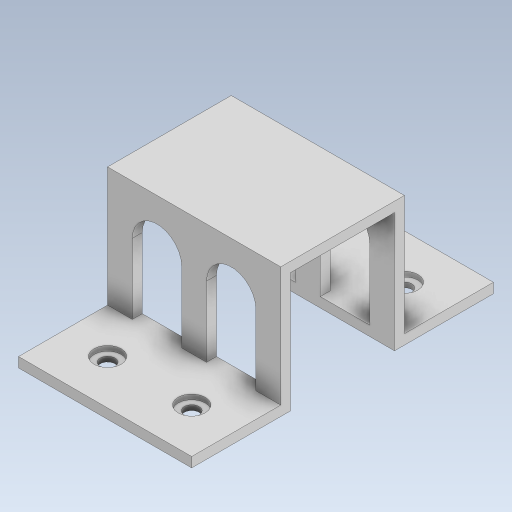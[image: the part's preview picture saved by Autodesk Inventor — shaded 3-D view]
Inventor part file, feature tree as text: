
AUTODESK INVENTOR PART (.ipt)
format: ipt  version: 2023.5 (Build 275446000, 446)  size: 423,424 bytes
history: native  units: in
note: dims shown in document units (in); Inventor stores cm internally (conversion verified against a paired STEP export)
features: extrude x10, sketch x8
ambient origin geometry x8: Origin, YZ Plane, XZ Plane, XY Plane, X Axis, Y Axis, Z Axis, Center Point
bodies: Solid1 (feature_tree)
feature tree (18):
  extrude  "Extrusion1"  Depth=0.7874in
  extrude  "Extrusion2"  Depth=0.0787in
  extrude  "Extrusion3"  Depth=0.0787in
  extrude  "Extrusion4"  Depth=0.0787in
  extrude  "Extrusion5"  Depth=0.7087in TaperAngle=0.0deg
  sketch  "Sketch6"  dims[d15=0.1181in d16=0.3543in]
  extrude  "Extrusion6"  Depth=0.3543in
  extrude  "Extrusion7"  Depth=0.1181in
  sketch  "Sketch7"  dims[d17=0.3543in d18=0.1181in]
  extrude  "Extrusion8"  Depth=0.9843in
  extrude  "Extrusion9"  Depth=0.9843in
  extrude  "Extrusion10"  Depth=0.0787in TaperAngle=0.0deg
  sketch  "Sketch1"  dims[d0=1.378in d1=0.7874in]
  sketch  "Sketch2"  dims[d2=0.0787in d3=0.0in d4=0.0787in]
  sketch  "Sketch3"  dims[d5=0.9528in d6=0.0in d7=0.0787in]
  sketch  "Sketch4"  dims[d8=0.9055in d9=0.0in d10=0.0787in]
  sketch  "Sketch5"  dims[d11=0.9528in d12=0.0in d13=0.7087in d14=0.0in]
  sketch  "Sketch8"  dims[d19=0.6693in d20=0.2165in d21=0.2165in d22=0.0787in d23=0.0in d24=0.0394in d25=0.0in d26=0.1181in d27=0.3543in d28=0.3543in d29=0.1181in d30=0.6693in d31=0.2165in d32=0.2165in d33=0.0787in d34=0.0in d35=0.0394in d36=0.0in d37=0.3937in d38=0.3937in d39=0.3937in d40=0.9843in d41=0.0in]
